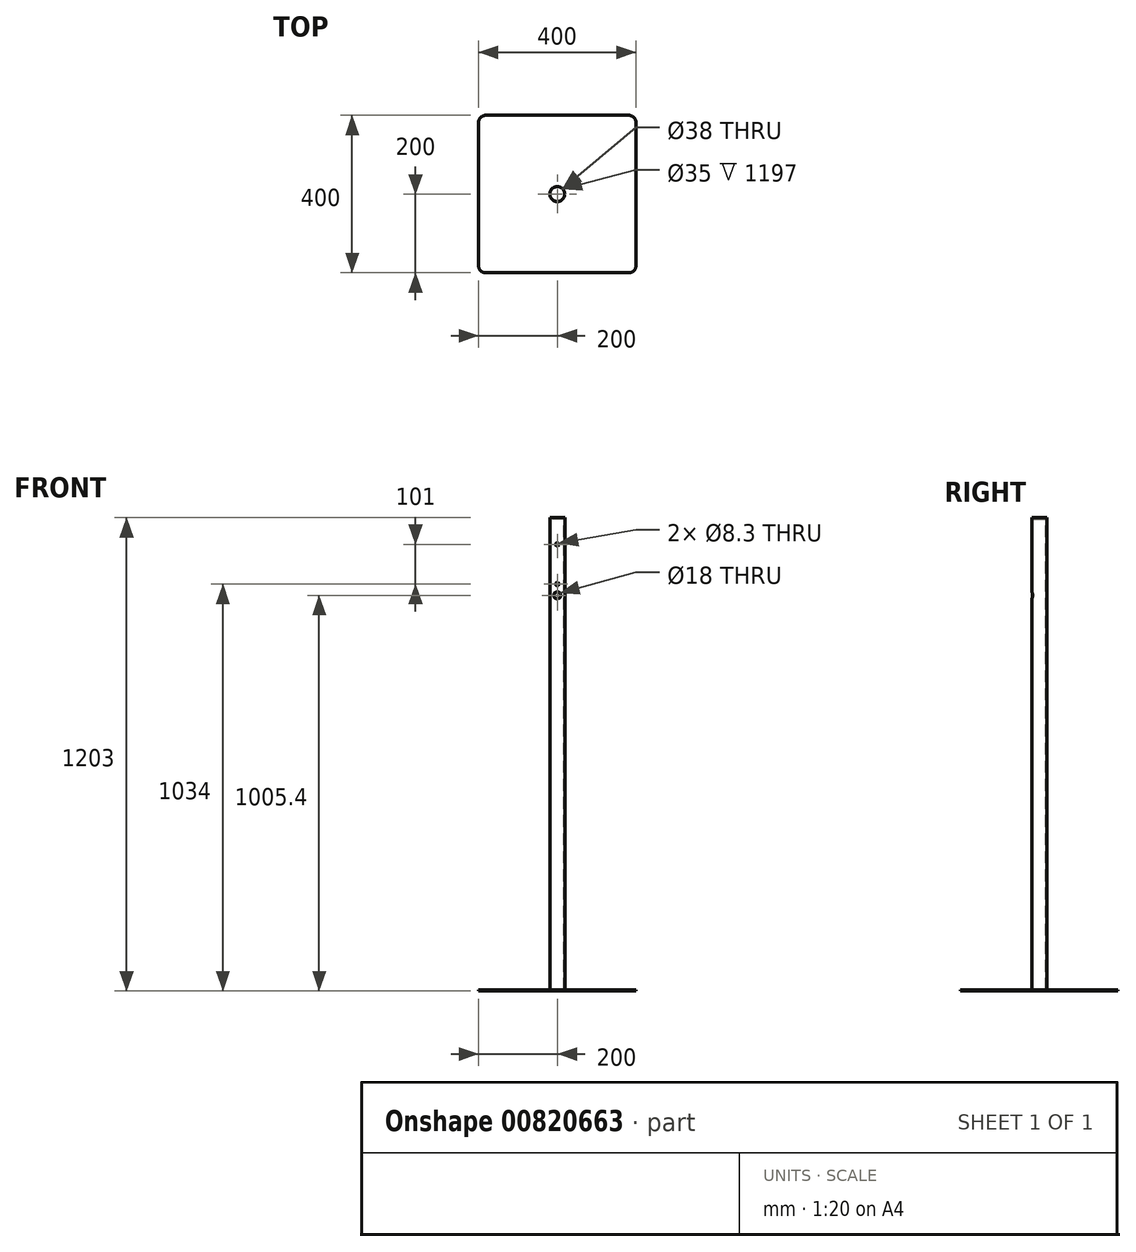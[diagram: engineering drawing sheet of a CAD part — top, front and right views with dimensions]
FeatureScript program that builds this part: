
annotation { "Feature Type Name" : "Feature", "Feature Type Description" : "" }
export const myFeature = defineFeature(function(context is Context, id is Id, definition is map)
    precondition{}
    {
        {
            var Q0;
            Q0=qCreatedBy(makeId("Front.planeOp"),FACE);
            var sketch = newSketch(context, id + "F0", { "sketchPlane" : qUnion([Q0])});
            skLineSegment(sketch, "E0", {"start": v(0, 43.51) * mm, "end": v(0, -52.26) * mm, "construction": true});
            skLineSegment(sketch, "E1.bottom", {"start": v(0, 1156.58) * mm, "end": v(-19, 1156.58) * mm});
            skLineSegment(sketch, "E1.top", {"start": v(0, -43.42) * mm, "end": v(-19, -43.42) * mm});
            skLineSegment(sketch, "E1.left", {"start": v(0, 1156.58) * mm, "end": v(0, 1092.73) * mm});
            skLineSegment(sketch, "E1.right", {"start": v(-19, 1156.58) * mm, "end": v(-19, -41.83) * mm});
            skLineSegment(sketch, "E2.bottom", {"start": v(-17.5, 1156.58) * mm, "end": v(0, 1156.58) * mm});
            skLineSegment(sketch, "E2.top", {"start": v(-17.5, -43.42) * mm, "end": v(0, -43.42) * mm});
            skLineSegment(sketch, "E2.left", {"start": v(-17.5, 1156.58) * mm, "end": v(-17.5, -43.42) * mm});
            skPoint(sketch, "E3", {"position": v(0, 987.58) * mm});
            skCircle(sketch, "E4", {"center": v(0, 987.58) * mm, "radius": 4.15 * mm});
            skLineSegment(sketch, "E5.trimOffspring", {"start": v(0, 983.43) * mm, "end": v(0, 967.98) * mm});
            skPoint(sketch, "E6", {"position": v(0, 1088.58) * mm});
            skCircle(sketch, "E7", {"center": v(0, 1088.58) * mm, "radius": 4.15 * mm});
            skLineSegment(sketch, "E8.trimOffspring", {"start": v(0, 1084.43) * mm, "end": v(0, 991.73) * mm});
            skCircle(sketch, "E9", {"center": v(0, 958.98) * mm, "radius": 9 * mm});
            skLineSegment(sketch, "E10.trimOffspring", {"start": v(0, 949.98) * mm, "end": v(0, -43.42) * mm});
            skLineSegment(sketch, "E11", {"start": v(-19, -41.83) * mm, "end": v(-19, -43.42) * mm});
            skSolve(sketch);
        }
        {
            var Q0;
            Q0=makeQuery(id+"F0.imprint","IMPRINT",FACE,{"disambiguationData":[TD([[makeQuery(id+"F0.imprint","IMPRINT",EDGE,{"derivedFrom":sQuery(id+"F0.wireOp",EDGE,"E1.bottom")}),1.0]])]});
            var Q1;
            Q1=sQuery(id+"F0.wireOp",EDGE,"E1.left");
            revolve(context, id + "F1", {"entities" : qUnion([Q0]), "axis" : qUnion([Q1]), "revolveType" : RevolveType.FULL});
        }
        {
            var Q0;
            {var subQ0=sQuery(id+"F0.wireOp",EDGE,"E4");var subQ1=makeQuery(id+"F0.imprint","INTERSECT",VERTEX,{"derivedFrom":[sQuery(id+"F0.wireOp",EDGE,"E1.left"),subQ0]});Q0=makeQuery(id+"F0.imprint","IMPRINT",FACE,{"disambiguationData":[TD([[makeQuery(id+"F0.imprint","IMPRINT",EDGE,{"disambiguationData":[TD([[subQ1,-1.0]])],"derivedFrom":subQ0}),1.0]])]});}
            extrude(context, id + "F2", {"entities" : qUnion([Q0]), "operationType" : NewBodyOperationType.REMOVE, "endBound" : BoundingType.THROUGH_ALL, "depth" : 25 * mm, "offsetDistance" : 25 * mm});
        }
        {
            var Q0;
            {var subQ0=sQuery(id+"F0.wireOp",EDGE,"E7");var subQ1=makeQuery(id+"F0.imprint","INTERSECT",VERTEX,{"derivedFrom":[sQuery(id+"F0.wireOp",EDGE,"E1.left"),subQ0]});Q0=makeQuery(id+"F0.imprint","IMPRINT",FACE,{"disambiguationData":[TD([[makeQuery(id+"F0.imprint","IMPRINT",EDGE,{"disambiguationData":[TD([[subQ1,-1.0]])],"derivedFrom":subQ0}),1.0]])]});}
            extrude(context, id + "F3", {"entities" : qUnion([Q0]), "operationType" : NewBodyOperationType.REMOVE, "endBound" : BoundingType.THROUGH_ALL, "depth" : 25 * mm, "offsetDistance" : 25 * mm});
        }
        {
            var Q0;
            {var subQ0=sQuery(id+"F0.wireOp",EDGE,"E9");var subQ1=makeQuery(id+"F0.imprint","INTERSECT",VERTEX,{"derivedFrom":[sQuery(id+"F0.wireOp",EDGE,"E5.trimOffspring"),subQ0]});Q0=makeQuery(id+"F0.imprint","IMPRINT",FACE,{"disambiguationData":[TD([[makeQuery(id+"F0.imprint","IMPRINT",EDGE,{"disambiguationData":[TD([[subQ1,-1.0]])],"derivedFrom":subQ0}),1.0]])]});}
            extrude(context, id + "F4", {"entities" : qUnion([Q0]), "operationType" : NewBodyOperationType.REMOVE, "endBound" : BoundingType.THROUGH_ALL, "depth" : 25 * mm, "offsetDistance" : 25 * mm});
        }
        {
            var Q0;
            Q0=makeQuery(id+"F1.opRevolve","SWEPT_FACE",FACE,{"disambiguationData":[OSD([sQuery(id+"F0.wireOp",EDGE,"E1.top")])]});
            var sketch = newSketch(context, id + "F5", { "sketchPlane" : qUnion([Q0])});
            skLineSegment(sketch, "E12.bottom", {"start": v(-182, 200) * mm, "end": v(182, 200) * mm});
            skLineSegment(sketch, "E12.top", {"start": v(-182, -200) * mm, "end": v(182, -200) * mm});
            skLineSegment(sketch, "E12.left", {"start": v(-200, 182) * mm, "end": v(-200, -182) * mm});
            skLineSegment(sketch, "E12.right", {"start": v(200, 182) * mm, "end": v(200, -182) * mm});
            skPoint(sketch, "E13.visualSharp", {"position": v(-200, 200) * mm});
            skArc(sketch, "E13.filletArc", {"start": v(-182, 200) * mm, "mid": v(-194.73, 194.73) * mm, "end": v(-200, 182) * mm});
            skPoint(sketch, "E14.visualSharp", {"position": v(200, 200) * mm});
            skArc(sketch, "E14.filletArc", {"start": v(200, 182) * mm, "mid": v(194.73, 194.73) * mm, "end": v(182, 200) * mm});
            skPoint(sketch, "E15.visualSharp", {"position": v(-200, -200) * mm});
            skArc(sketch, "E15.filletArc", {"start": v(-200, -182) * mm, "mid": v(-194.73, -194.73) * mm, "end": v(-182, -200) * mm});
            skPoint(sketch, "E16.visualSharp", {"position": v(200, -200) * mm});
            skArc(sketch, "E16.filletArc", {"start": v(182, -200) * mm, "mid": v(194.73, -194.73) * mm, "end": v(200, -182) * mm});
            skSolve(sketch);
        }
        {
            var Q0;
            Q0=makeQuery(id+"F5.imprint","IMPRINT",FACE,{"disambiguationData":[TD([[makeQuery(id+"F5.imprint","IMPRINT",EDGE,{"derivedFrom":sQuery(id+"F5.wireOp",EDGE,"E12.bottom")}),-1.0]])]});
            extrude(context, id + "F6", {"entities" : qUnion([Q0]), "depth" : 3 * mm, "offsetDistance" : 25 * mm});
        }
        {
            var Q0;
            Q0=makeQuery(id+"F1.opRevolve","SWEPT_FACE",FACE,{"disambiguationData":[OSD([sQuery(id+"F0.wireOp",EDGE,"E1.bottom")])]});
            var sketch = newSketch(context, id + "F7", { "sketchPlane" : qUnion([Q0])});
            skCircle(sketch, "E17", {"center": v(0, 0) * mm, "radius": 19 * mm});
            skSolve(sketch);
        }
        {
            var Q0;
            Q0 = qSketchRegion(id + "F7", true);
            extrude(context, id + "F8", {"entities" : qUnion([Q0]), "operationType" : NewBodyOperationType.ADD, "oppositeDirection" : true, "depth" : 3 * mm, "offsetDistance" : 25 * mm});
        }
    });
